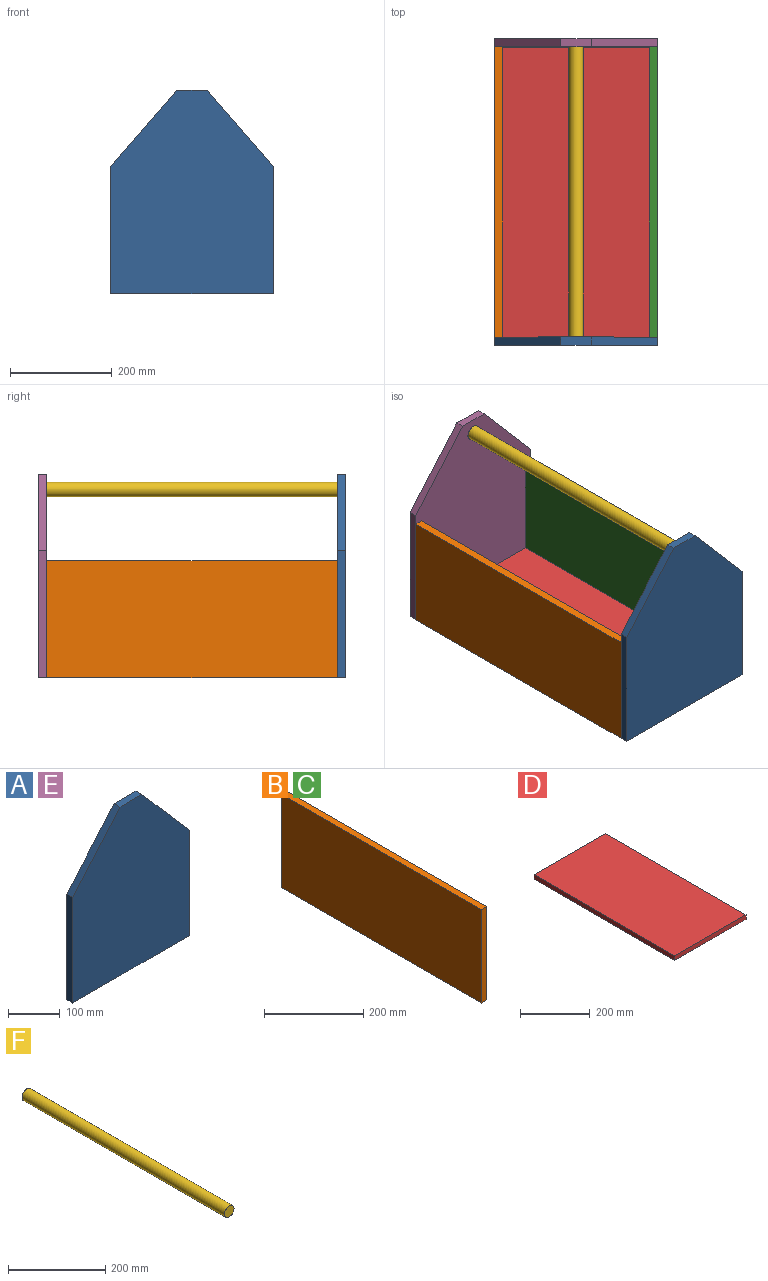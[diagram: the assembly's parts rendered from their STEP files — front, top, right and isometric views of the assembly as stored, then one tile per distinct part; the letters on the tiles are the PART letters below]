
ASSEMBLY  parts=6 mates=5
PART A: 10 faces, bbox 320x16x400 mm
  f0: plane 400x320mm, normal (0,1,0), area 107793.1mm2, adj f2,f3,f4,f5,f6,f7,f8
  f1: plane 400x320mm, normal (0,-1,0), area 108500mm2, adj f2,f3,f4,f5,f6,f7
  f2: plane 60x16mm, normal (0,0,1), area 960mm2, adj f0,f1,f6,f7
  f3: plane 250x16mm, normal (1,0,0), area 4000mm2, adj f0,f1,f5,f7
  f4: plane 250x16mm, normal (-1,0,0), area 4000mm2, adj f0,f1,f5,f6
  f5: plane 320x16mm, normal (0,0,-1), area 5120mm2, adj f0,f1,f3,f4
  f6: plane 150x130mm, normal (-0.76,0,0.65), area 3175.9mm2, adj f0,f1,f2,f4
  f7: plane 150x130mm, normal (0.76,0,0.65), area 3175.9mm2, adj f0,f1,f2,f3
  f8: cylinder r=15mm len=30mm, axis (0,1,0), area 1131mm2, adj f0,f9
  f9: plane 30x30mm, normal (0,1,0), area 706.9mm2, adj f8
PART B: 6 faces, bbox 16x570x230 mm
  f0: plane 570x230mm, normal (-1,0,0), area 131100mm2, adj f1,f3,f4,f5
  f1: plane 230x16mm, normal (0,-1,0), area 3680mm2, adj f0,f2,f4,f5
  f2: plane 570x230mm, normal (1,0,0), area 131100mm2, adj f1,f3,f4,f5
  f3: plane 230x16mm, normal (0,1,0), area 3680mm2, adj f0,f2,f4,f5
  f4: plane 570x16mm, normal (0,0,1), area 9120mm2, adj f0,f1,f2,f3
  f5: plane 570x16mm, normal (0,0,-1), area 9120mm2, adj f0,f1,f2,f3
PART C: same geometry as B
PART D: 6 faces, bbox 288x570x16 mm
  f0: plane 570x16mm, normal (1,0,0), area 9120mm2, adj f1,f3,f4,f5
  f1: plane 288x16mm, normal (0,1,0), area 4608mm2, adj f0,f2,f4,f5
  f2: plane 570x16mm, normal (-1,0,0), area 9120mm2, adj f1,f3,f4,f5
  f3: plane 288x16mm, normal (0,-1,0), area 4608mm2, adj f0,f2,f4,f5
  f4: plane 570x288mm, normal (0,0,-1), area 164160mm2, adj f0,f1,f2,f3
  f5: plane 570x288mm, normal (0,0,1), area 164160mm2, adj f0,f1,f2,f3
PART E: same geometry as A
PART F: 3 faces, bbox 28x590x28 mm
  f0: cylinder r=14mm len=590mm, axis (0,-1,0), area 51899.1mm2, adj f1,f2
  f1: plane 28x28mm, normal (0,1,0), area 615.8mm2, adj f0
  f2: plane 28x28mm, normal (0,-1,0), area 615.8mm2, adj f0
PLACE A t=(0,-285,-5)mm
PLACE B t=(-304,-285,-5)mm
PLACE C rot(axis=(1,0,0),0deg) t=(0,-285,-5)mm
PLACE D t=(-16,-269,16)mm
PLACE E rot(axis=(0,0,-1),180deg) t=(0,285,-5)mm
PLACE F t=(0,-295,-5)mm
MATE fastened B.f2 <-> D.f2  axis (1,0,0) through (-144,0,-5)mm
MATE fastened F.f0 <-> A.f8  axis (0,-1,0) through (0,-295,365)mm
MATE fastened A.f0 <-> D.f3  axis (0,1,0) through (0,-285,-5)mm
MATE fastened C.f0 <-> D.f0  axis (-1,0,0) through (144,0,-5)mm
MATE fastened E.f0 <-> D.f1  axis (0,-1,0) through (0,285,-5)mm
